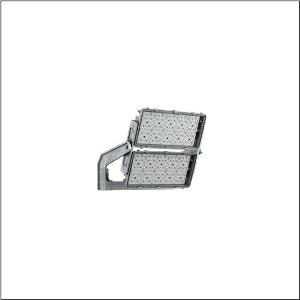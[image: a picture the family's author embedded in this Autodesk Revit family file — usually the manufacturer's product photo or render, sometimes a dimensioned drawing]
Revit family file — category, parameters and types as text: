
# Revit family: floodlight_fl_11_maxi_remote___rs07_5xa779514k01ba_6340
name_source: partatom
category: Lighting Fixtures
units: mm (PartAtom-declared; Revit-internal decimal feet)

## family parameters
Cut with Voids When Loaded = No
Host = Face
Light Source = No
Part Type = Normal
Room Calculation Point = No
Round Connector Dimension = Use Diameter
Shared = No

## types (1)
- --- (1 x LED, 75300 lm, 707.9 W, 5700K)
    Apparent Load = 708 VA
    CIE Flux Codes = 80 93 99 100 99
    Color Rendering = 90
    Color Temperature = 5700K
    Default Elevation = 1800 mm
    Description = Floodlight FL 11  maxi  Remote floodlight; light control with lens of PMMA; cover panel of toughened safety glass, transparent; light distribution: RS07, rotationally symmetric direct distribution, LEDcolour temperature: 5700K, rated luminous flux: 75.300lm, colour rendering: CRI > 90, light colour: 957; luminous efficacy: 106lm/W; brightness control: DMX+RDM; with terminal, 8-pole, max. 2.5mm², mains connection: 220..240V/380..400V AC, 50/60Hz, surge voltage resistance: line to ground: 10kV, ECG replaceable separately, LED unit replaceable without ESD environment, dustproof LED module, dimming range 10..100%; 708W floodlight with 2x LED unit of diecast aluminium, coated grey; length: 713mm / width: 651mm / height: 338mm; mounting bracket, of diecast aluminium, uncoated, natural, equipment: Longlife, protection rating (complete): IP66; insulation class (complete): insulation class I (protective earthing); certification: CE, ENEC, VDE; ball protection: ball impact resistance with accessories, impact resistance: IK07; only for outdoor installations, rated ambient temperature 10°C, permissible operating ambient temperature: -40..+40°C, permissible storage temperature: -40..+85°C; packaging unit: 1 piece

Light Distribution: RS07
    Height = 320 mm
    Lamp = 1 x LED
    Lamp Light Flux = 75300 lm
    Lamp Power = 707.9 W
    Lamp count = 1
    Length = 712 mm
    Luminous efficacy = 106 lm/W
    Manufacturer = Siteco
    ModVariant = No
    Model = 5XA779514K01BA
    Mounting Place = Ceiling
    Mounting Type = Surface mounted
    Number of Poles = 1
    OnlyDefault = Yes
    Power Factor = 1
    Product Name = Floodlight FL 11 maxi Remote | RS07
    Product group = floodlight | ceiling mounted
    ProductGroupID = 302
    Protection Class = Protection class I
    Protection Degree = IP 66
    RLX_Detail_Level = 1
    RLX_Emergency_Light_Flux = 0 lm
    RLX_Emergency_Type = 0
    RLX_Emergency_Type_DB = No
    RlxData = <blob elided: 41225 chars, md5=4be29e96>
    Socket = socket
    Standby Power = 0 W
    System Light Flux = 75300 lm
    System Power = 708 W
    Type Comments = factory setting: luminous flux: 100 % | dim-lin: 254 | 740 mA
    Type Image = l_1006788.jpg
    URL = http://relux.com
    VarID = @adj_114523
    Voltage = 0 V
    Weight = 0.00 kg
    Width = 655 mm

## geometry (parser evidence)
native form markers: Blend x4, Sweep x11
no freeform markers — native parametric forms only
